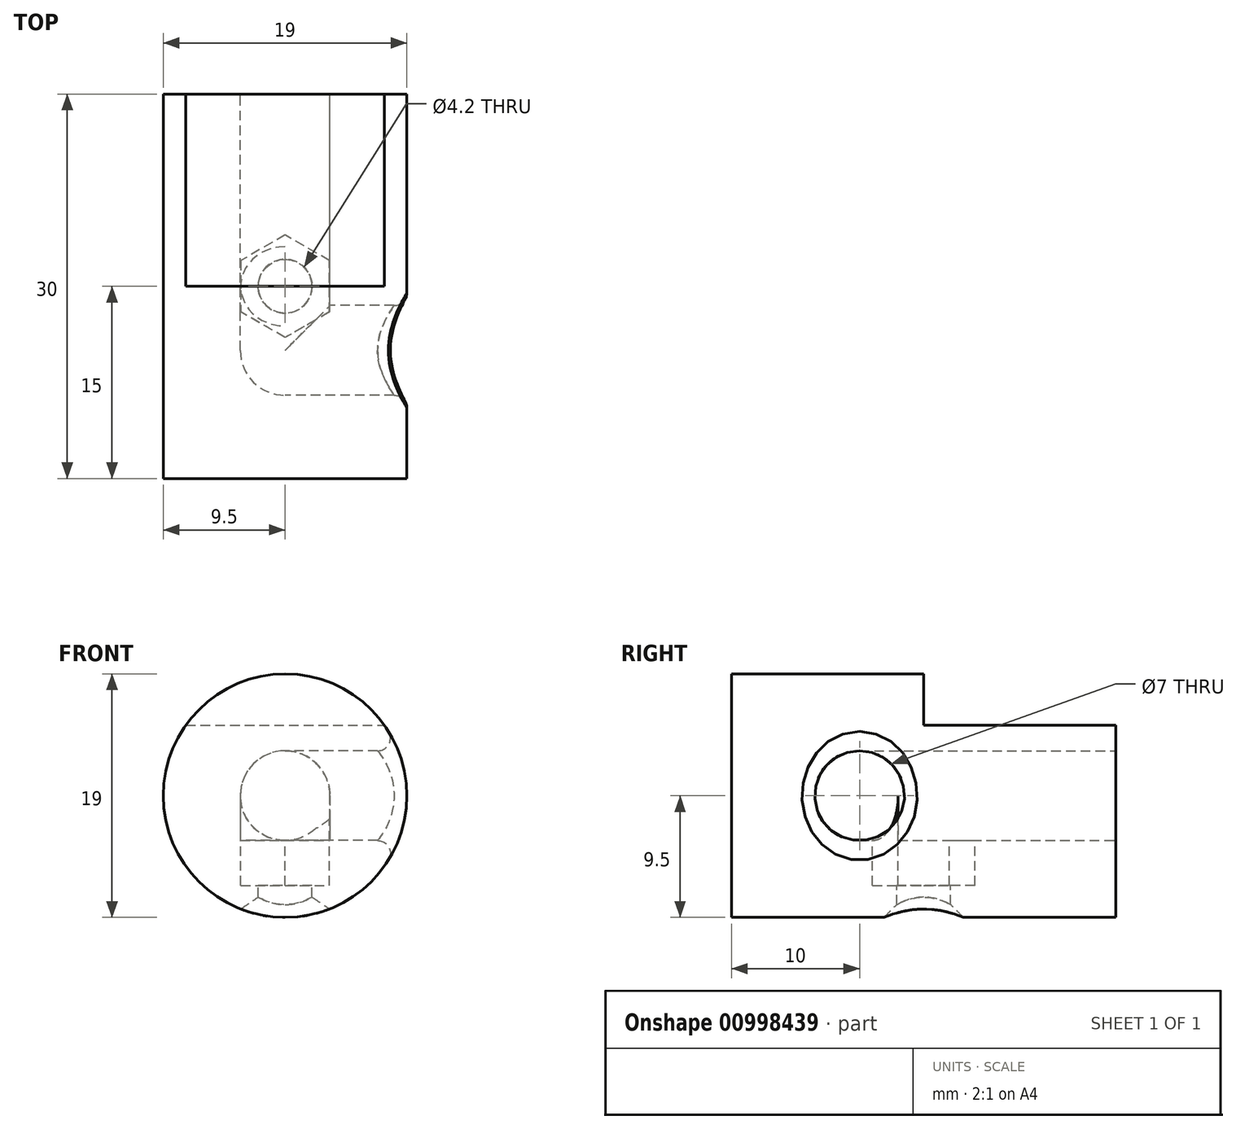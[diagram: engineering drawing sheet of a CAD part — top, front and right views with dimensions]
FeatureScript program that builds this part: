
annotation { "Feature Type Name" : "Feature", "Feature Type Description" : "" }
export const myFeature = defineFeature(function(context is Context, id is Id, definition is map)
    precondition{}
    {
        {
            var Q0;
            Q0=qCreatedBy(makeId("Front.planeOp"),FACE);
            var sketch = newSketch(context, id + "F0", { "sketchPlane" : qUnion([Q0])});
            skCircle(sketch, "E0", {"center": v(0, 0) * mm, "radius": 9.5 * mm});
            skPoint(sketch, "E1", {"position": v(0, -9.5) * mm});
            skLineSegment(sketch, "E2", {"start": v(-7.75, 5.5) * mm, "end": v(7.75, 5.5) * mm});
            skCircle(sketch, "E3", {"center": v(0, 0) * mm, "radius": 3.5 * mm});
            skSolve(sketch);
        }
        {
            var Q0;
            {var subQ0=sQuery(id+"F0.wireOp",EDGE,"E2");Q0=makeQuery(id+"F0.imprint","IMPRINT",FACE,{"disambiguationData":[TD([[makeQuery(id+"F0.imprint","IMPRINT",EDGE,{"derivedFrom":subQ0}),-1.0]])]});}
            var Q1;
            Q1=makeQuery(id+"F0.imprint","IMPRINT",FACE,{"disambiguationData":[TD([[makeQuery(id+"F0.imprint","IMPRINT",EDGE,{"derivedFrom":sQuery(id+"F0.wireOp",EDGE,"E3")}),1.0]])]});
            extrude(context, id + "F1", {"entities" : qUnion([Q0, Q1]), "oppositeDirection" : true, "depth" : 15 * mm, "offsetDistance" : 25 * mm});
        }
        {
            var Q0;
            {var subQ0=sQuery(id+"F0.wireOp",EDGE,"E2");Q0=makeQuery(id+"F0.imprint","IMPRINT",FACE,{"disambiguationData":[TD([[makeQuery(id+"F0.imprint","IMPRINT",EDGE,{"derivedFrom":subQ0}),1.0]])]});}
            var Q1;
            Q1=makeQuery(id+"F0.imprint","IMPRINT",FACE,{"disambiguationData":[TD([[makeQuery(id+"F0.imprint","IMPRINT",EDGE,{"derivedFrom":sQuery(id+"F0.wireOp",EDGE,"E3")}),1.0]])]});
            var Q2;
            {var subQ0=sQuery(id+"F0.wireOp",EDGE,"E2");Q2=makeQuery(id+"F0.imprint","IMPRINT",FACE,{"disambiguationData":[TD([[makeQuery(id+"F0.imprint","IMPRINT",EDGE,{"derivedFrom":subQ0}),-1.0]])]});}
            extrude(context, id + "F2", {"entities" : qUnion([Q0, Q1, Q2]), "operationType" : NewBodyOperationType.ADD, "depth" : 10 * mm, "offsetDistance" : 25 * mm});
        }
        {
            var Q0;
            Q0=makeQuery(id+"F1.opExtrude","CAP_FACE",FACE,{"disambiguationData":[OSD([sQuery(id+"F0.wireOp",EDGE,"E0"),sQuery(id+"F0.wireOp",EDGE,"E2")])],"isStart":false});
            var sketch = newSketch(context, id + "F3", { "sketchPlane" : qUnion([Q0])});
            skCircle(sketch, "E4", {"center": v(0, 0) * mm, "radius": 3.5 * mm});
            skSolve(sketch);
        }
        {
            var Q0;
            Q0=makeQuery(id+"F3.imprint","IMPRINT",FACE,{"disambiguationData":[TD([[makeQuery(id+"F3.imprint","IMPRINT",EDGE,{"derivedFrom":sQuery(id+"F3.wireOp",EDGE,"E4")}),1.0]])]});
            var Q1;
            Q1=sQuery(id+"F3.wireOp",EDGE,"E4");
            extrude(context, id + "F4", {"entities" : qUnion([Q0]), "operationType" : NewBodyOperationType.REMOVE, "surfaceEntities" : qUnion([Q1]), "oppositeDirection" : true, "depth" : 20 * mm, "offsetDistance" : 25 * mm});
        }
        {
            var Q0;
            Q0=qCreatedBy(makeId("Right.planeOp"),FACE);
            var sketch = newSketch(context, id + "F5", { "sketchPlane" : qUnion([Q0])});
            skLineSegment(sketch, "E5", {"start": v(0, 0) * mm, "end": v(-5, 0) * mm, "construction": true});
            skCircle(sketch, "E6", {"center": v(-5, 0) * mm, "radius": 3.5 * mm});
            skSolve(sketch);
        }
        {
            var Q0;
            Q0 = qSketchRegion(id + "F5", true);
            extrude(context, id + "F6", {"entities" : qUnion([Q0]), "operationType" : NewBodyOperationType.REMOVE, "depth" : 25 * mm, "offsetDistance" : 25 * mm});
        }
        {
            var Q0;
            Q0=makeQuery(id+"F6.boolean.opBoolean","COPY",FACE,{"derivedFrom":makeQuery(id+"F6.opExtrude","CAP_FACE",FACE,{"disambiguationData":[OSD([sQuery(id+"F5.wireOp",EDGE,"E6")])],"isStart":true})});
            var Q1;
            Q1=makeQuery(id+"F6.boolean.opBoolean","INTERSECT",EDGE,{"derivedFrom":[makeQuery(id+"F4.boolean.opBoolean","COPY",FACE,{"derivedFrom":makeQuery(id+"F4.opExtrude","CAP_FACE",FACE,{"disambiguationData":[OSD([sQuery(id+"F3.wireOp",EDGE,"E4")])],"isStart":false})}),makeQuery(id+"F6.opExtrude","CAP_FACE",FACE,{"disambiguationData":[OSD([sQuery(id+"F5.wireOp",EDGE,"E6")])],"isStart":true})]});
            revolve(context, id + "F7", {"operationType" : NewBodyOperationType.REMOVE, "surfaceOperationType" : NewSurfaceOperationType.NEW, "entities" : qUnion([Q0]), "axis" : qUnion([Q1]), "revolveType" : RevolveType.ONE_DIRECTION, "angle" : 90 * degree});
        }
        {
            var Q0;
            Q0=qCreatedBy(makeId("Top.planeOp"),FACE);
            var sketch = newSketch(context, id + "F8", { "sketchPlane" : qUnion([Q0])});
            skCircle(sketch, "E7", {"center": v(0, 0) * mm, "radius": 4 * mm});
            skLineSegment(sketch, "E8", {"start": v(0, 0) * mm, "end": v(0, 4) * mm});
            skLineSegment(sketch, "E9.1.0", {"start": v(0, 0) * mm, "end": v(-3.46, 2) * mm});
            skLineSegment(sketch, "E9.2.0", {"start": v(0, 0) * mm, "end": v(-3.46, -2) * mm});
            skLineSegment(sketch, "E9.3.0", {"start": v(0, 0) * mm, "end": v(0, -4) * mm});
            skLineSegment(sketch, "E9.4.0", {"start": v(0, 0) * mm, "end": v(3.46, -2) * mm});
            skLineSegment(sketch, "E9.5.0", {"start": v(0, 0) * mm, "end": v(3.46, 2) * mm});
            skLineSegment(sketch, "E10", {"start": v(0, 4) * mm, "end": v(3.46, 2) * mm});
            skLineSegment(sketch, "E11", {"start": v(3.46, 2) * mm, "end": v(3.46, -2) * mm});
            skLineSegment(sketch, "E12", {"start": v(3.46, -2) * mm, "end": v(0, -4) * mm});
            skLineSegment(sketch, "E13", {"start": v(0, -4) * mm, "end": v(-3.46, -2) * mm});
            skLineSegment(sketch, "E14", {"start": v(-3.46, -2) * mm, "end": v(-3.46, 2) * mm});
            skLineSegment(sketch, "E15", {"start": v(-3.46, 2) * mm, "end": v(0, 4) * mm});
            skCircle(sketch, "E16", {"center": v(0, 0) * mm, "radius": 2.1 * mm});
            skSolve(sketch);
        }
        {
            var Q0;
            {var subQ1=sQuery(id+"F8.wireOp",EDGE,"E8");var subQ3=sQuery(id+"F8.wireOp",EDGE,"E16");var subQ4=makeQuery(id+"F8.imprint","INTERSECT",VERTEX,{"derivedFrom":[subQ1,subQ3]});Q0=makeQuery(id+"F8.imprint","IMPRINT",FACE,{"disambiguationData":[TD([[makeQuery(id+"F8.imprint","IMPRINT",EDGE,{"disambiguationData":[TD([[subQ4,-1.0]])],"derivedFrom":subQ3}),1.0]])]});}
            var Q1;
            {var subQ1=sQuery(id+"F8.wireOp",EDGE,"E9.1.0");var subQ3=sQuery(id+"F8.wireOp",EDGE,"E16");var subQ4=makeQuery(id+"F8.imprint","INTERSECT",VERTEX,{"derivedFrom":[subQ1,subQ3]});Q1=makeQuery(id+"F8.imprint","IMPRINT",FACE,{"disambiguationData":[TD([[makeQuery(id+"F8.imprint","IMPRINT",EDGE,{"disambiguationData":[TD([[subQ4,-1.0]])],"derivedFrom":subQ3}),1.0]])]});}
            var Q2;
            {var subQ1=sQuery(id+"F8.wireOp",EDGE,"E9.2.0");var subQ3=sQuery(id+"F8.wireOp",EDGE,"E16");var subQ4=makeQuery(id+"F8.imprint","INTERSECT",VERTEX,{"derivedFrom":[subQ1,subQ3]});Q2=makeQuery(id+"F8.imprint","IMPRINT",FACE,{"disambiguationData":[TD([[makeQuery(id+"F8.imprint","IMPRINT",EDGE,{"disambiguationData":[TD([[subQ4,-1.0]])],"derivedFrom":subQ3}),1.0]])]});}
            var Q3;
            {var subQ1=sQuery(id+"F8.wireOp",EDGE,"E9.3.0");var subQ3=sQuery(id+"F8.wireOp",EDGE,"E16");var subQ4=makeQuery(id+"F8.imprint","INTERSECT",VERTEX,{"derivedFrom":[subQ1,subQ3]});Q3=makeQuery(id+"F8.imprint","IMPRINT",FACE,{"disambiguationData":[TD([[makeQuery(id+"F8.imprint","IMPRINT",EDGE,{"disambiguationData":[TD([[subQ4,-1.0]])],"derivedFrom":subQ3}),1.0]])]});}
            var Q4;
            {var subQ1=sQuery(id+"F8.wireOp",EDGE,"E9.4.0");var subQ3=sQuery(id+"F8.wireOp",EDGE,"E16");var subQ4=makeQuery(id+"F8.imprint","INTERSECT",VERTEX,{"derivedFrom":[subQ1,subQ3]});Q4=makeQuery(id+"F8.imprint","IMPRINT",FACE,{"disambiguationData":[TD([[makeQuery(id+"F8.imprint","IMPRINT",EDGE,{"disambiguationData":[TD([[subQ4,-1.0]])],"derivedFrom":subQ3}),1.0]])]});}
            var Q5;
            {var subQ1=sQuery(id+"F8.wireOp",EDGE,"E8");var subQ3=sQuery(id+"F8.wireOp",EDGE,"E16");var subQ4=makeQuery(id+"F8.imprint","INTERSECT",VERTEX,{"derivedFrom":[subQ1,subQ3]});Q5=makeQuery(id+"F8.imprint","IMPRINT",FACE,{"disambiguationData":[TD([[makeQuery(id+"F8.imprint","IMPRINT",EDGE,{"disambiguationData":[TD([[subQ4,1.0]])],"derivedFrom":subQ3}),1.0]])]});}
            var Q6;
            Q6=sQuery(id+"F8.wireOp",EDGE,"E16");
            extrude(context, id + "F9", {"entities" : qUnion([Q0, Q1, Q2, Q3, Q4, Q5]), "operationType" : NewBodyOperationType.REMOVE, "surfaceEntities" : qUnion([Q6]), "oppositeDirection" : true, "depth" : 25 * mm, "offsetDistance" : 25 * mm});
        }
        {
            var Q0;
            {var subQ0=sQuery(id+"F8.wireOp",EDGE,"E12");Q0=makeQuery(id+"F8.imprint","IMPRINT",FACE,{"disambiguationData":[TD([[makeQuery(id+"F8.imprint","IMPRINT",EDGE,{"derivedFrom":subQ0}),-1.0]])]});}
            var Q1;
            {var subQ0=sQuery(id+"F8.wireOp",EDGE,"E13");Q1=makeQuery(id+"F8.imprint","IMPRINT",FACE,{"disambiguationData":[TD([[makeQuery(id+"F8.imprint","IMPRINT",EDGE,{"derivedFrom":subQ0}),-1.0]])]});}
            var Q2;
            {var subQ0=sQuery(id+"F8.wireOp",EDGE,"E14");Q2=makeQuery(id+"F8.imprint","IMPRINT",FACE,{"disambiguationData":[TD([[makeQuery(id+"F8.imprint","IMPRINT",EDGE,{"derivedFrom":subQ0}),-1.0]])]});}
            var Q3;
            {var subQ0=sQuery(id+"F8.wireOp",EDGE,"E15");Q3=makeQuery(id+"F8.imprint","IMPRINT",FACE,{"disambiguationData":[TD([[makeQuery(id+"F8.imprint","IMPRINT",EDGE,{"derivedFrom":subQ0}),-1.0]])]});}
            var Q4;
            {var subQ0=sQuery(id+"F8.wireOp",EDGE,"E10");Q4=makeQuery(id+"F8.imprint","IMPRINT",FACE,{"disambiguationData":[TD([[makeQuery(id+"F8.imprint","IMPRINT",EDGE,{"derivedFrom":subQ0}),-1.0]])]});}
            var Q5;
            {var subQ0=sQuery(id+"F8.wireOp",EDGE,"E11");Q5=makeQuery(id+"F8.imprint","IMPRINT",FACE,{"disambiguationData":[TD([[makeQuery(id+"F8.imprint","IMPRINT",EDGE,{"derivedFrom":subQ0}),-1.0]])]});}
            extrude(context, id + "F10", {"entities" : qUnion([Q0, Q1, Q2, Q3, Q4, Q5]), "operationType" : NewBodyOperationType.REMOVE, "oppositeDirection" : true, "depth" : 7 * mm, "offsetDistance" : 25 * mm});
        }
        {
            var Q0;
            Q0=makeQuery(id+"F1.opExtrude","CAP_FACE",FACE,{"disambiguationData":[OSD([sQuery(id+"F0.wireOp",EDGE,"E0"),sQuery(id+"F0.wireOp",EDGE,"E2")])],"isStart":false});
            var sketch = newSketch(context, id + "F11", { "sketchPlane" : qUnion([Q0])});
            skLineSegment(sketch, "E17", {"start": v(0, 0) * mm, "end": v(3.5, 0) * mm, "construction": true});
            skLineSegment(sketch, "E18.bottom", {"start": v(3.5, 0) * mm, "end": v(-3.5, 0) * mm});
            skLineSegment(sketch, "E18.top", {"start": v(3.5, -3.5) * mm, "end": v(-3.5, -3.5) * mm});
            skLineSegment(sketch, "E18.left", {"start": v(3.5, 0) * mm, "end": v(3.5, -3.5) * mm});
            skLineSegment(sketch, "E18.right", {"start": v(-3.5, 0) * mm, "end": v(-3.5, -3.5) * mm});
            skSolve(sketch);
        }
        {
            var Q0;
            {var subQ0=sQuery(id+"F11.wireOp",EDGE,"E18.right");Q0=makeQuery(id+"F11.imprint","IMPRINT",FACE,{"disambiguationData":[TD([[makeQuery(id+"F11.imprint","IMPRINT",EDGE,{"derivedFrom":subQ0}),1.0]])]});}
            var Q1;
            {var subQ0=sQuery(id+"F11.wireOp",EDGE,"E18.left");Q1=makeQuery(id+"F11.imprint","IMPRINT",FACE,{"disambiguationData":[TD([[makeQuery(id+"F11.imprint","IMPRINT",EDGE,{"derivedFrom":subQ0}),-1.0]])]});}
            extrude(context, id + "F12", {"entities" : qUnion([Q0, Q1]), "operationType" : NewBodyOperationType.REMOVE, "oppositeDirection" : true, "depth" : 17 * mm, "offsetDistance" : 25 * mm});
        }
        {
            var Q0;
            {var subQ0=sQuery(id+"F0.wireOp",EDGE,"E0");Q0=makeQuery(id+"F6.boolean.opBoolean","INTERSECT",EDGE,{"derivedFrom":[makeQuery(id+"F2.boolean.opBoolean","MERGE",FACE,{"derivedFrom":[makeQuery(id+"F1.opExtrude","SWEPT_FACE",FACE,{"disambiguationData":[OSD([subQ0])]}),makeQuery(id+"F2.opExtrude","SWEPT_FACE",FACE,{"disambiguationData":[OSD([subQ0])]})]}),makeQuery(id+"F6.opExtrude","SWEPT_FACE",FACE,{"disambiguationData":[OSD([sQuery(id+"F5.wireOp",EDGE,"E6")])]})]});}
            fillet(context, id + "F13", {"entities" : qUnion([Q0]), "radius" : 1 * mm, "tangentPropagation" : true, "allowEdgeOverflow" : false});
        }
        {
            var Q0;
            {var subQ0=sQuery(id+"F0.wireOp",EDGE,"E0");Q0=makeQuery(id+"F9.boolean.opBoolean","INTERSECT",EDGE,{"derivedFrom":[makeQuery(id+"F2.boolean.opBoolean","MERGE",FACE,{"derivedFrom":[makeQuery(id+"F1.opExtrude","SWEPT_FACE",FACE,{"disambiguationData":[OSD([subQ0])]}),makeQuery(id+"F2.opExtrude","SWEPT_FACE",FACE,{"disambiguationData":[OSD([subQ0])]})]}),makeQuery(id+"F9.opExtrude","SWEPT_FACE",FACE,{"disambiguationData":[OSD([sQuery(id+"F8.wireOp",EDGE,"E16")])]})]});}
            chamfer(context, id + "F14", {"entities" : qUnion([Q0]), "width" : 1 * mm, "tangentPropagation" : true});
        }
        {
            var Q0;
            Q0=makeQuery(id+"F2.opExtrude","CAP_FACE",FACE,{"disambiguationData":[OSD([sQuery(id+"F0.wireOp",EDGE,"E0")])],"isStart":false});
            extrude(context, id + "F15", {"entities" : qUnion([Q0]), "operationType" : NewBodyOperationType.ADD, "depth" : 5 * mm, "offsetDistance" : 25 * mm});
        }
    });
